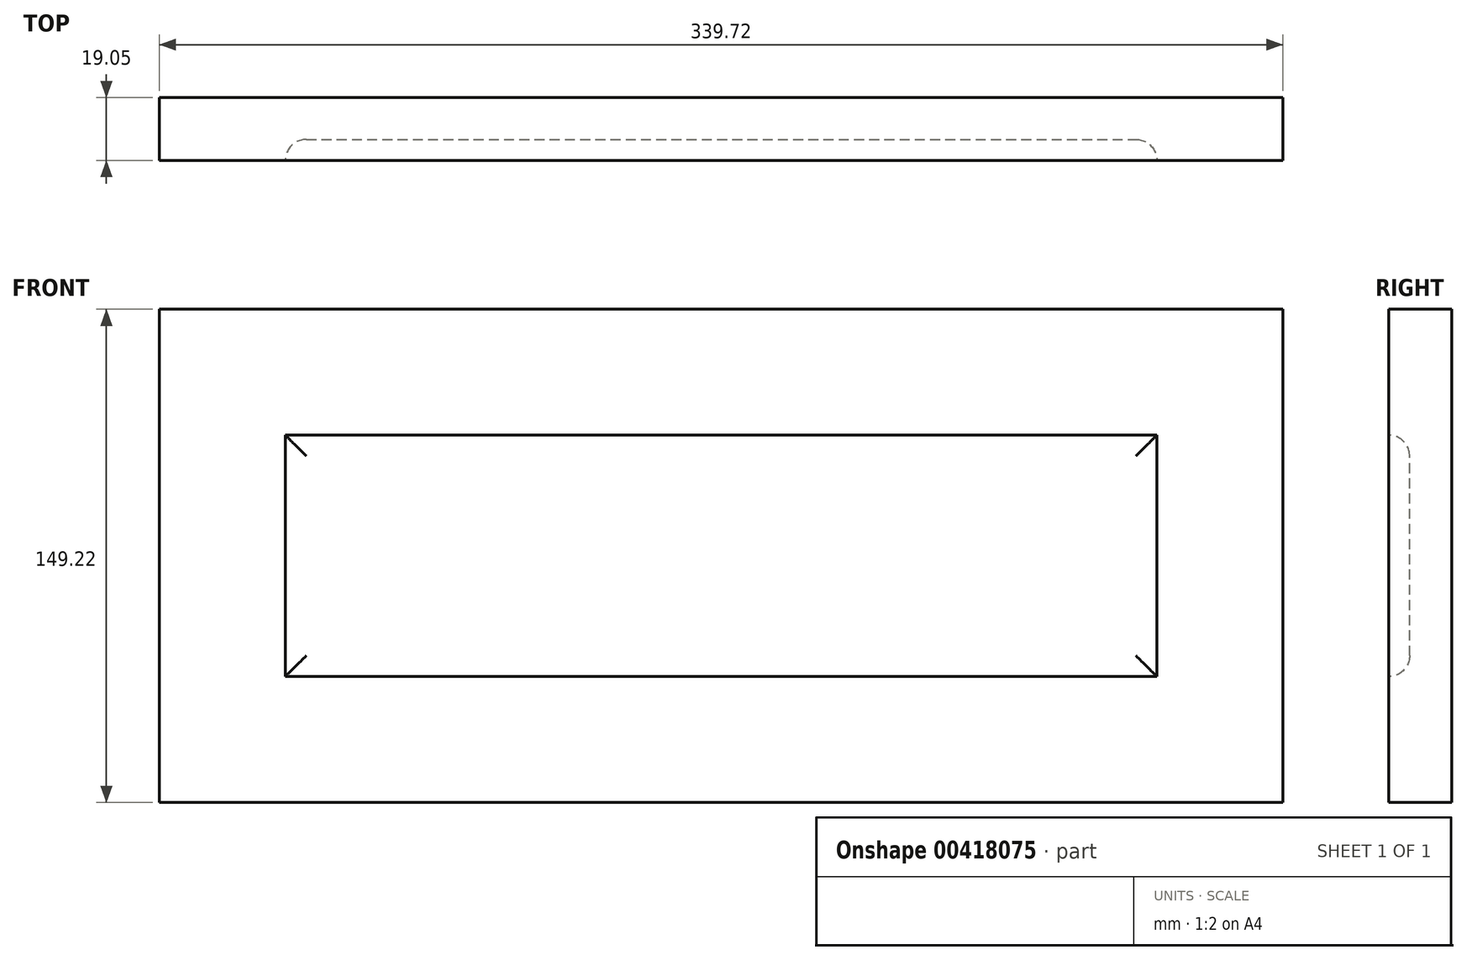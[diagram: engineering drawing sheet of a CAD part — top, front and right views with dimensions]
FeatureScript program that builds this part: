
annotation { "Feature Type Name" : "Feature", "Feature Type Description" : "" }
export const myFeature = defineFeature(function(context is Context, id is Id, definition is map)
    precondition{}
    {
        {
            var Q0;
            Q0=qCreatedBy(makeId("Front.planeOp"),FACE);
            var sketch = newSketch(context, id + "F0", { "sketchPlane" : qUnion([Q0])});
            skLineSegment(sketch, "E0.bottom", {"start": v(-169.86, -74.61) * mm, "end": v(169.86, -74.61) * mm});
            skLineSegment(sketch, "E0.top", {"start": v(-169.86, 74.61) * mm, "end": v(169.86, 74.61) * mm});
            skLineSegment(sketch, "E0.left", {"start": v(-169.86, -74.61) * mm, "end": v(-169.86, 74.61) * mm});
            skLineSegment(sketch, "E0.right", {"start": v(169.86, -74.61) * mm, "end": v(169.86, 74.61) * mm});
            skPoint(sketch, "E0.middle", {"position": v(0, 0) * mm});
            skLineSegment(sketch, "E1.bottom", {"start": v(-131.76, -36.51) * mm, "end": v(131.76, -36.51) * mm});
            skLineSegment(sketch, "E1.top", {"start": v(-131.76, 36.51) * mm, "end": v(131.76, 36.51) * mm});
            skLineSegment(sketch, "E1.left", {"start": v(-131.76, -36.51) * mm, "end": v(-131.76, 36.51) * mm});
            skLineSegment(sketch, "E1.right", {"start": v(131.76, -36.51) * mm, "end": v(131.76, 36.51) * mm});
            skSolve(sketch);
        }
        {
            var Q0;
            Q0=makeQuery(id+"F0.imprint","IMPRINT",FACE,{"disambiguationData":[TD([[makeQuery(id+"F0.imprint","IMPRINT",EDGE,{"derivedFrom":sQuery(id+"F0.wireOp",EDGE,"E0.bottom")}),1.0]])]});
            extrude(context, id + "F1", {"entities" : qUnion([Q0]), "depth" : 19.05 * mm});
        }
        {
            var Q0;
            Q0=makeQuery(id+"F0.imprint","IMPRINT",FACE,{"disambiguationData":[TD([[makeQuery(id+"F0.imprint","IMPRINT",EDGE,{"derivedFrom":sQuery(id+"F0.wireOp",EDGE,"E1.bottom")}),1.0]])]});
            extrude(context, id + "F2", {"entities" : qUnion([Q0]), "operationType" : NewBodyOperationType.ADD, "depth" : 12.7 * mm});
        }
        {
            var Q0;
            Q0=makeQuery(id+"F2.opExtrude","CAP_EDGE",EDGE,{"disambiguationData":[OSD([sQuery(id+"F0.wireOp",EDGE,"E1.top")])],"isStart":false});
            var Q1;
            Q1=makeQuery(id+"F2.opExtrude","CAP_FACE",FACE,{"disambiguationData":[OSD([sQuery(id+"F0.wireOp",EDGE,"E1.bottom"),sQuery(id+"F0.wireOp",EDGE,"E1.top"),sQuery(id+"F0.wireOp",EDGE,"E1.left"),sQuery(id+"F0.wireOp",EDGE,"E1.right")])],"isStart":false});
            fillet(context, id + "F3", {"entities" : qUnion([Q0, Q1]), "radius" : 6.35 * mm, "tangentPropagation" : true, "allowEdgeOverflow" : false});
        }
    });
